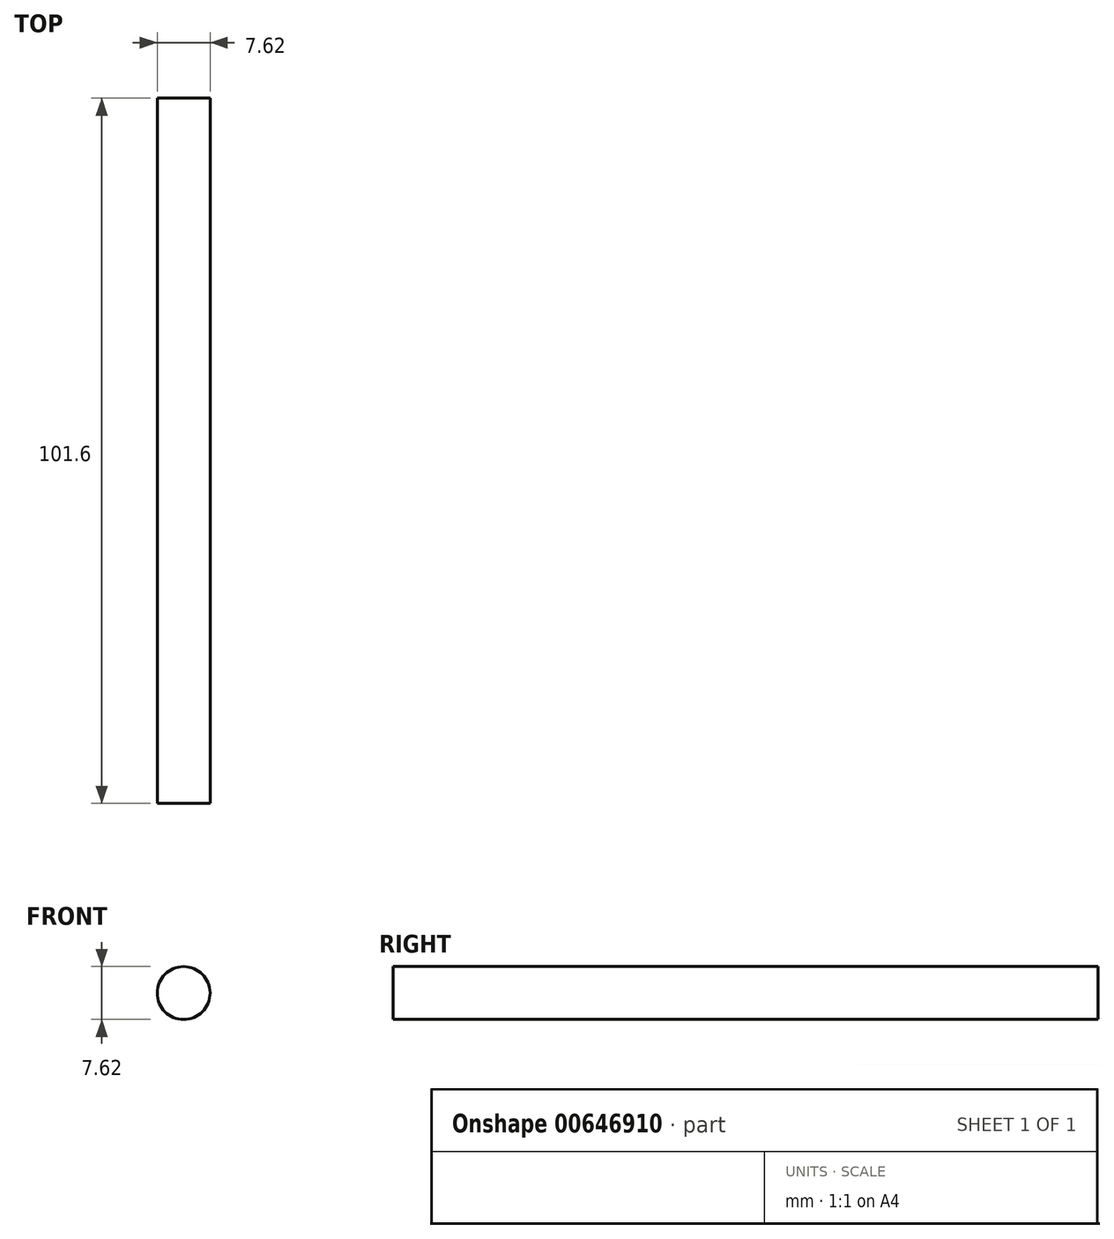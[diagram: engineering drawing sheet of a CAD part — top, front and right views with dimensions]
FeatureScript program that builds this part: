
annotation { "Feature Type Name" : "Feature", "Feature Type Description" : "" }
export const myFeature = defineFeature(function(context is Context, id is Id, definition is map)
    precondition{}
    {
        {
            var Q0;
            Q0=qCreatedBy(makeId("Front.planeOp"),FACE);
            var sketch = newSketch(context, id + "F0", { "sketchPlane" : qUnion([Q0])});
            skCircle(sketch, "E0", {"center": v(0, 0) * mm, "radius": 3.81 * mm});
            skSolve(sketch);
        }
        {
            var Q0;
            Q0 = qSketchRegion(id + "F0", true);
            extrude(context, id + "F1", {"entities" : qUnion([Q0]), "depth" : 101.6 * mm, "offsetDistance" : 25.4 * mm});
        }
    });
